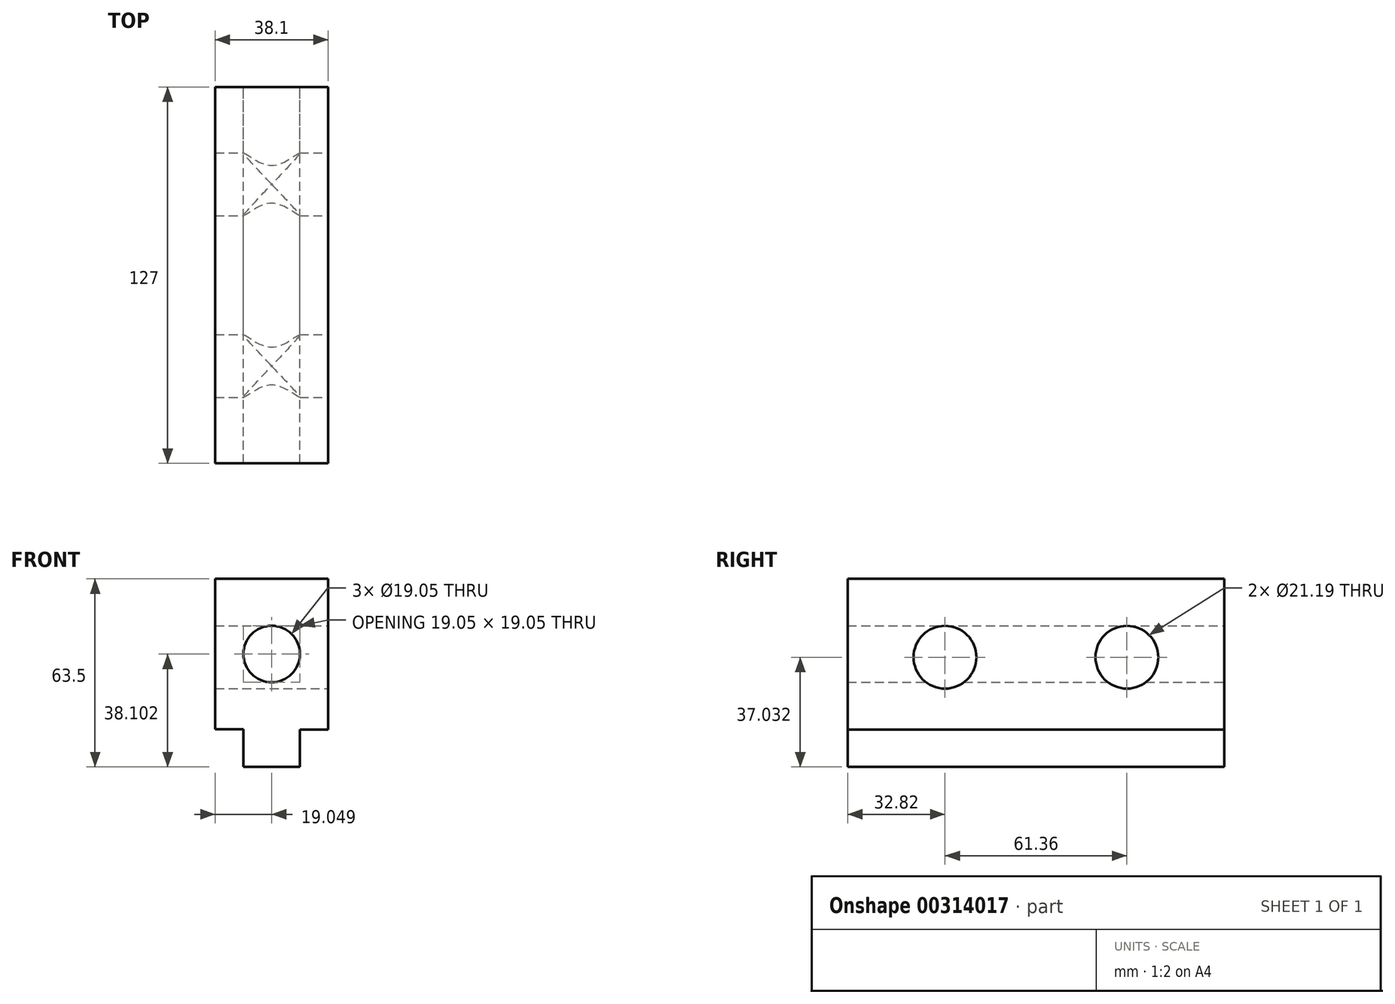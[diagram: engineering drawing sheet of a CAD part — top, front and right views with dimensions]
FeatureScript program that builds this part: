
annotation { "Feature Type Name" : "Feature", "Feature Type Description" : "" }
export const myFeature = defineFeature(function(context is Context, id is Id, definition is map)
    precondition{}
    {
        {
            var Q0;
            Q0=qCreatedBy(makeId("Front.planeOp"),FACE);
            var sketch = newSketch(context, id + "F0", { "sketchPlane" : qUnion([Q0])});
            skLineSegment(sketch, "E0", {"start": v(-25.94, 37.64) * mm, "end": v(-25.94, -13.16) * mm});
            skLineSegment(sketch, "E1", {"start": v(-25.94, 37.64) * mm, "end": v(12.16, 37.64) * mm});
            skLineSegment(sketch, "E2", {"start": v(12.16, 37.64) * mm, "end": v(12.16, -13.26) * mm});
            skLineSegment(sketch, "E3", {"start": v(-25.94, -13.16) * mm, "end": v(-16.42, -13.16) * mm});
            skLineSegment(sketch, "E4", {"start": v(12.16, -13.26) * mm, "end": v(2.62, -13.26) * mm});
            skLineSegment(sketch, "E5", {"start": v(-16.42, -13.16) * mm, "end": v(-16.42, -25.86) * mm});
            skLineSegment(sketch, "E6", {"start": v(-16.42, -25.86) * mm, "end": v(2.62, -25.86) * mm});
            skLineSegment(sketch, "E7", {"start": v(2.62, -13.26) * mm, "end": v(2.62, -25.86) * mm});
            skSolve(sketch);
        }
        {
            var Q0;
            Q0 = qSketchRegion(id + "F0", true);
            extrude(context, id + "F1", {"entities" : qUnion([Q0]), "depth" : 127 * mm});
        }
        {
            var Q0;
            Q0=qCreatedBy(makeId("Right.planeOp"),FACE);
            var sketch = newSketch(context, id + "F2", { "sketchPlane" : qUnion([Q0])});
            skCircle(sketch, "E8", {"center": v(-442.56, 14.38) * mm, "radius": 104.33 * mm});
            skCircle(sketch, "E9", {"center": v(196.33, 10.43) * mm, "radius": 26.18 * mm});
            skCircle(sketch, "E10", {"center": v(-94.18, 11.17) * mm, "radius": 10.6 * mm});
            skCircle(sketch, "E11", {"center": v(-32.82, 11.17) * mm, "radius": 10.6 * mm});
            skSolve(sketch);
        }
        {
            var Q0;
            Q0 = qSketchRegion(id + "F2", true);
            extrude(context, id + "F3", {"entities" : qUnion([Q0]), "operationType" : NewBodyOperationType.REMOVE, "oppositeDirection" : true, "depth" : 38.1 * mm});
        }
        {
            var Q0;
            Q0=makeQuery(id+"F3.boolean.opBoolean","COPY",FACE,{"derivedFrom":makeQuery(id+"F3.opExtrude","CAP_FACE",FACE,{"disambiguationData":[OSD([sQuery(id+"F2.wireOp",EDGE,"E11")])],"isStart":true})});
            var Q1;
            Q1=makeQuery(id+"F3.boolean.opBoolean","COPY",FACE,{"derivedFrom":makeQuery(id+"F3.opExtrude","CAP_FACE",FACE,{"disambiguationData":[OSD([sQuery(id+"F2.wireOp",EDGE,"E10")])],"isStart":true})});
            extrude(context, id + "F4", {"entities" : qUnion([Q0, Q1]), "operationType" : NewBodyOperationType.REMOVE, "oppositeDirection" : true, "depth" : 38.1 * mm});
        }
        {
            var Q0;
            Q0=qCreatedBy(makeId("Front.planeOp"),FACE);
            var sketch = newSketch(context, id + "F5", { "sketchPlane" : qUnion([Q0])});
            skCircle(sketch, "E12", {"center": v(-6.9, 12.24) * mm, "radius": 9.53 * mm});
            skSolve(sketch);
        }
        {
            var Q0;
            Q0 = qSketchRegion(id + "F5", true);
            extrude(context, id + "F6", {"entities" : qUnion([Q0]), "operationType" : NewBodyOperationType.REMOVE, "depth" : 127 * mm});
        }
    });
